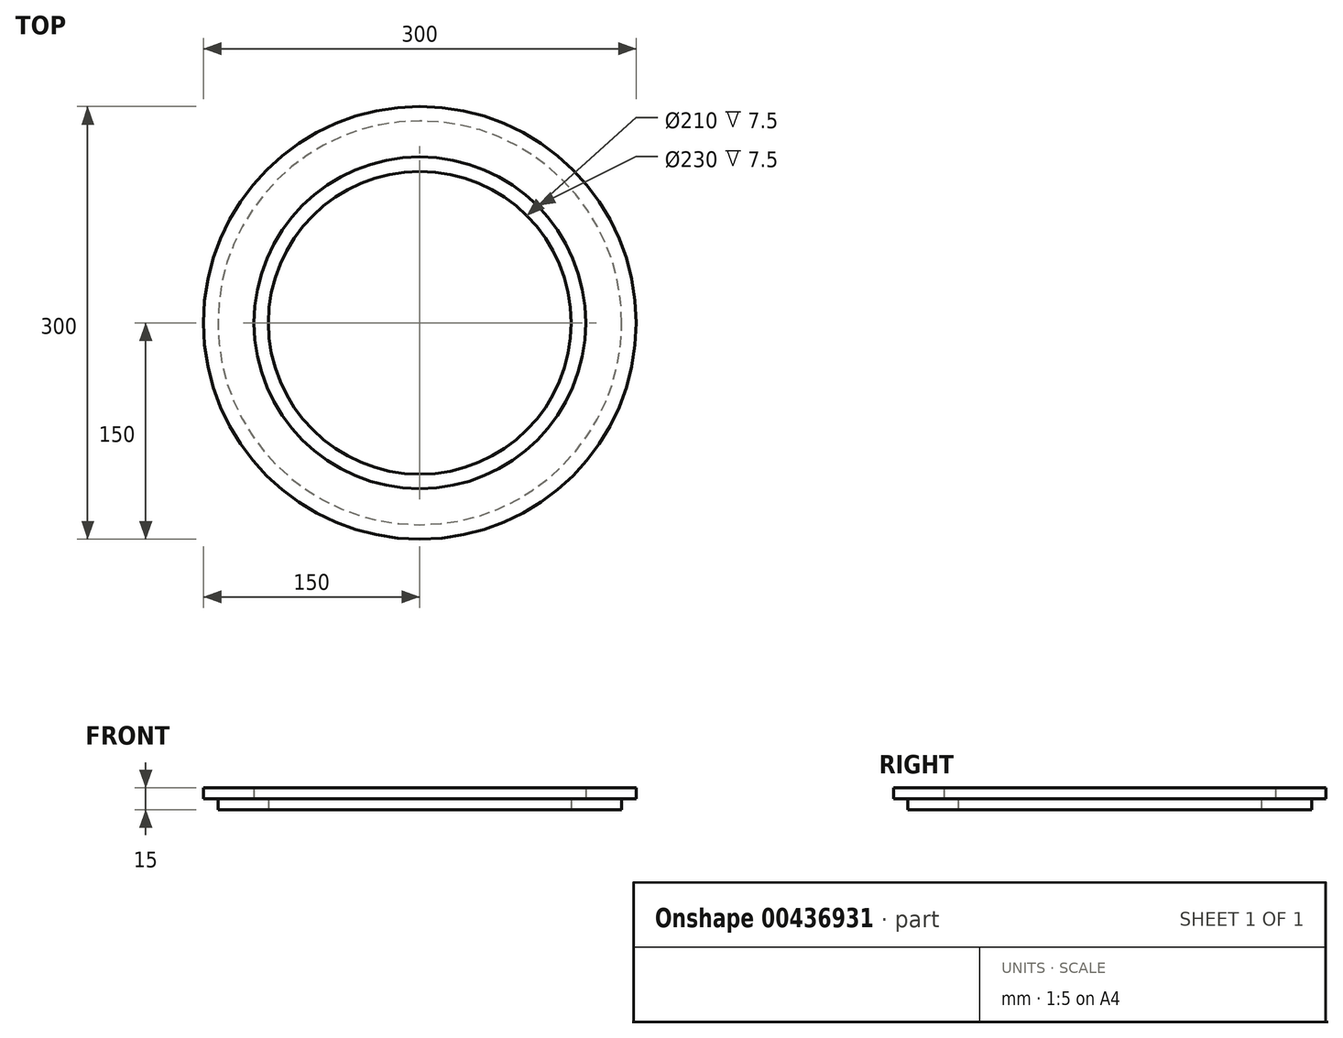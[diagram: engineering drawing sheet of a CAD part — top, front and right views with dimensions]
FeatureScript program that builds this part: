
annotation { "Feature Type Name" : "Feature", "Feature Type Description" : "" }
export const myFeature = defineFeature(function(context is Context, id is Id, definition is map)
    precondition{}
    {
        {
            var Q0;
            Q0=qCreatedBy(makeId("Front.planeOp"),FACE);
            var sketch = newSketch(context, id + "F0", { "sketchPlane" : qUnion([Q0])});
            skLineSegment(sketch, "E0", {"start": v(105, 0) * mm, "end": v(140, 0) * mm});
            skLineSegment(sketch, "E1", {"start": v(140, 0) * mm, "end": v(140, 7.5) * mm});
            skLineSegment(sketch, "E2", {"start": v(140, 7.5) * mm, "end": v(150, 7.5) * mm});
            skLineSegment(sketch, "E3", {"start": v(150, 7.5) * mm, "end": v(150, 15) * mm});
            skLineSegment(sketch, "E4", {"start": v(150, 15) * mm, "end": v(115, 15) * mm});
            skLineSegment(sketch, "E5", {"start": v(115, 15) * mm, "end": v(115, 7.5) * mm});
            skLineSegment(sketch, "E6", {"start": v(115, 7.5) * mm, "end": v(105, 7.5) * mm});
            skLineSegment(sketch, "E7", {"start": v(105, 7.5) * mm, "end": v(105, 0) * mm});
            skLineSegment(sketch, "E8", {"start": v(0, 0) * mm, "end": v(0, 115.63) * mm, "construction": true});
            skSolve(sketch);
        }
        {
            var Q0;
            Q0=makeQuery(id+"F0.imprint","IMPRINT",FACE,{"disambiguationData":[TD([[makeQuery(id+"F0.imprint","IMPRINT",EDGE,{"derivedFrom":sQuery(id+"F0.wireOp",EDGE,"E0")}),1.0]])]});
            var Q1;
            Q1=sQuery(id+"F0.wireOp",EDGE,"E8");
            var Q2;
            Q2=sQuery(id+"F0.wireOp",EDGE,"E8");
            revolve(context, id + "F1", {"entities" : qUnion([Q0]), "surfaceEntities" : qUnion([Q1]), "axis" : qUnion([Q2]), "revolveType" : RevolveType.FULL});
        }
    });
